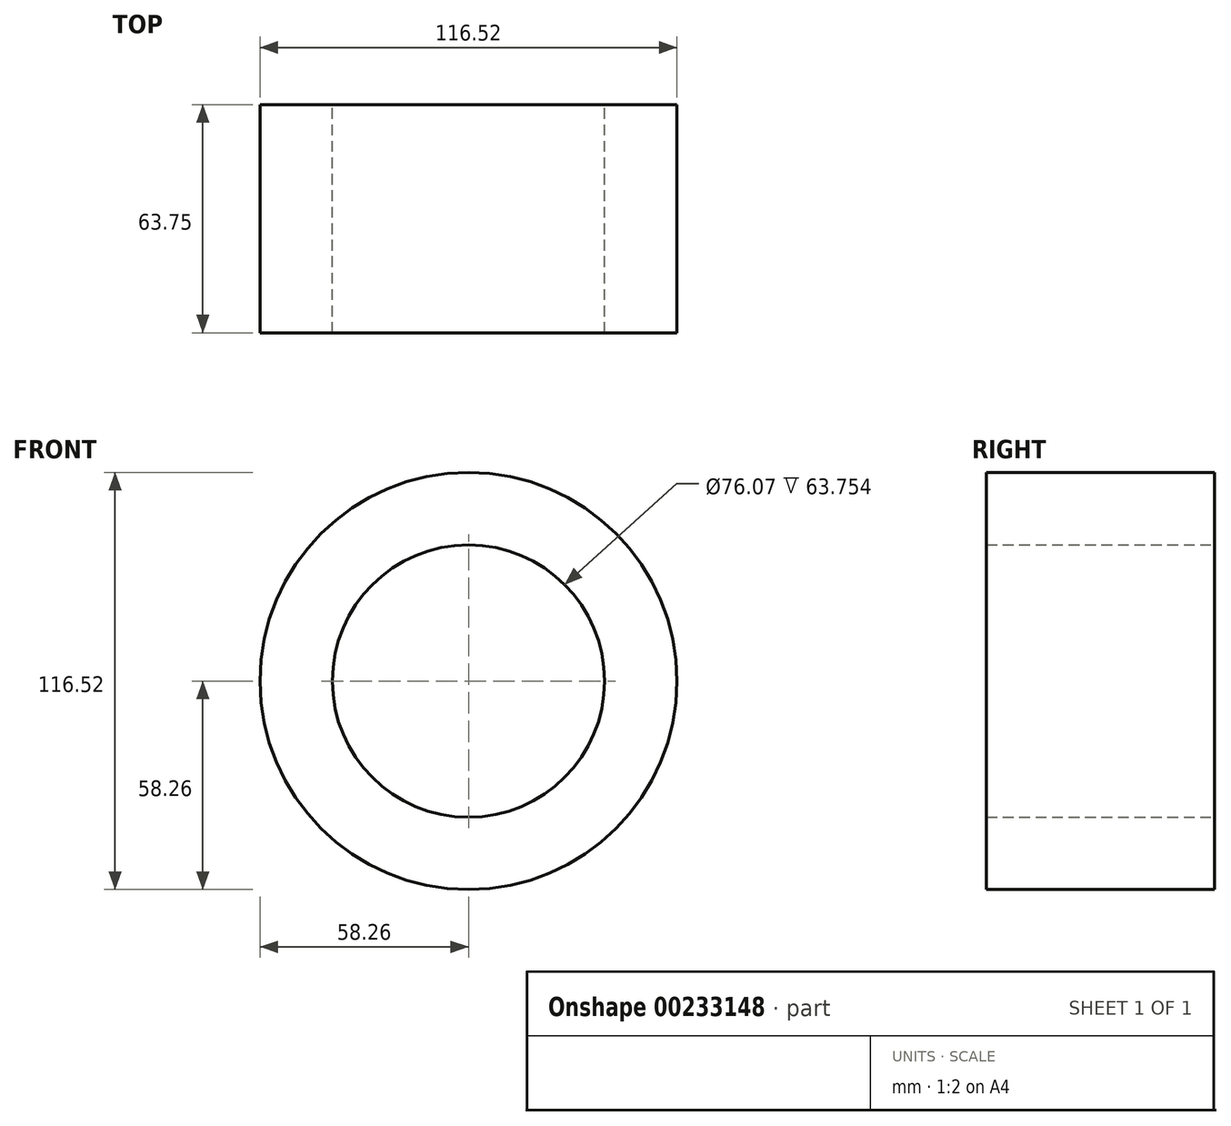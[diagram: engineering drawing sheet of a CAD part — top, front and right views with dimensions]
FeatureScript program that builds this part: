
annotation { "Feature Type Name" : "Feature", "Feature Type Description" : "" }
export const myFeature = defineFeature(function(context is Context, id is Id, definition is map)
    precondition{}
    {
        {
            var Q0;
            Q0=qCreatedBy(makeId("Front.planeOp"),FACE);
            var sketch = newSketch(context, id + "F0", { "sketchPlane" : qUnion([Q0])});
            skCircle(sketch, "E0", {"center": v(0, 0) * mm, "radius": 58.26 * mm});
            skCircle(sketch, "E1", {"center": v(0, 0) * mm, "radius": 38.04 * mm});
            skLineSegment(sketch, "E2", {"start": v(0, 0) * mm, "end": v(-29.74, 23.72) * mm});
            skLineSegment(sketch, "E3", {"start": v(0, 0) * mm, "end": v(-28.43, -25.27) * mm});
            skLineSegment(sketch, "E4", {"start": v(0, 0) * mm, "end": v(27.01, -26.78) * mm});
            skLineSegment(sketch, "E5", {"start": v(0, 0) * mm, "end": v(25.8, 27.94) * mm});
            skLineSegment(sketch, "E6", {"start": v(0, 0) * mm, "end": v(0, -38.04) * mm});
            skLineSegment(sketch, "E7", {"start": v(0, 0) * mm, "end": v(0, 38.04) * mm});
            skLineSegment(sketch, "E8", {"start": v(0, 0) * mm, "end": v(38.04, 0) * mm});
            skLineSegment(sketch, "E9", {"start": v(0, -1.86) * mm, "end": v(0, -38.04) * mm});
            skLineSegment(sketch, "E10", {"start": v(0, 0) * mm, "end": v(-38.04, 0) * mm});
            skCircle(sketch, "E11", {"center": v(0, 0) * mm, "radius": 29.1 * mm});
            skLineSegment(sketch, "E12.bottom", {"start": v(-15.71, 16.13) * mm, "end": v(15.71, 16.13) * mm});
            skLineSegment(sketch, "E12.top", {"start": v(-15.71, -16.13) * mm, "end": v(15.71, -16.13) * mm});
            skLineSegment(sketch, "E12.left", {"start": v(-15.71, 16.13) * mm, "end": v(-15.71, -16.13) * mm});
            skLineSegment(sketch, "E12.right", {"start": v(15.71, 16.13) * mm, "end": v(15.71, -16.13) * mm});
            skLineSegment(sketch, "E13.bottom", {"start": v(15.71, 16.13) * mm, "end": v(-15.71, 16.13) * mm});
            skLineSegment(sketch, "E13.top", {"start": v(15.71, -16.13) * mm, "end": v(-15.71, -16.13) * mm});
            skCircle(sketch, "E14", {"center": v(0, 0) * mm, "radius": 29.12 * mm});
            skSolve(sketch);
        }
        {
            var Q0;
            Q0 = qSketchRegion(id + "F0", true);
            extrude(context, id + "F1", {"entities" : qUnion([Q0]), "depth" : 34.54 * mm});
        }
        {
            var Q0;
            Q0 = qSketchRegion(id + "F0", true);
            extrude(context, id + "F2", {"entities" : qUnion([Q0]), "operationType" : NewBodyOperationType.ADD, "depth" : 63.75 * mm});
        }
    });
